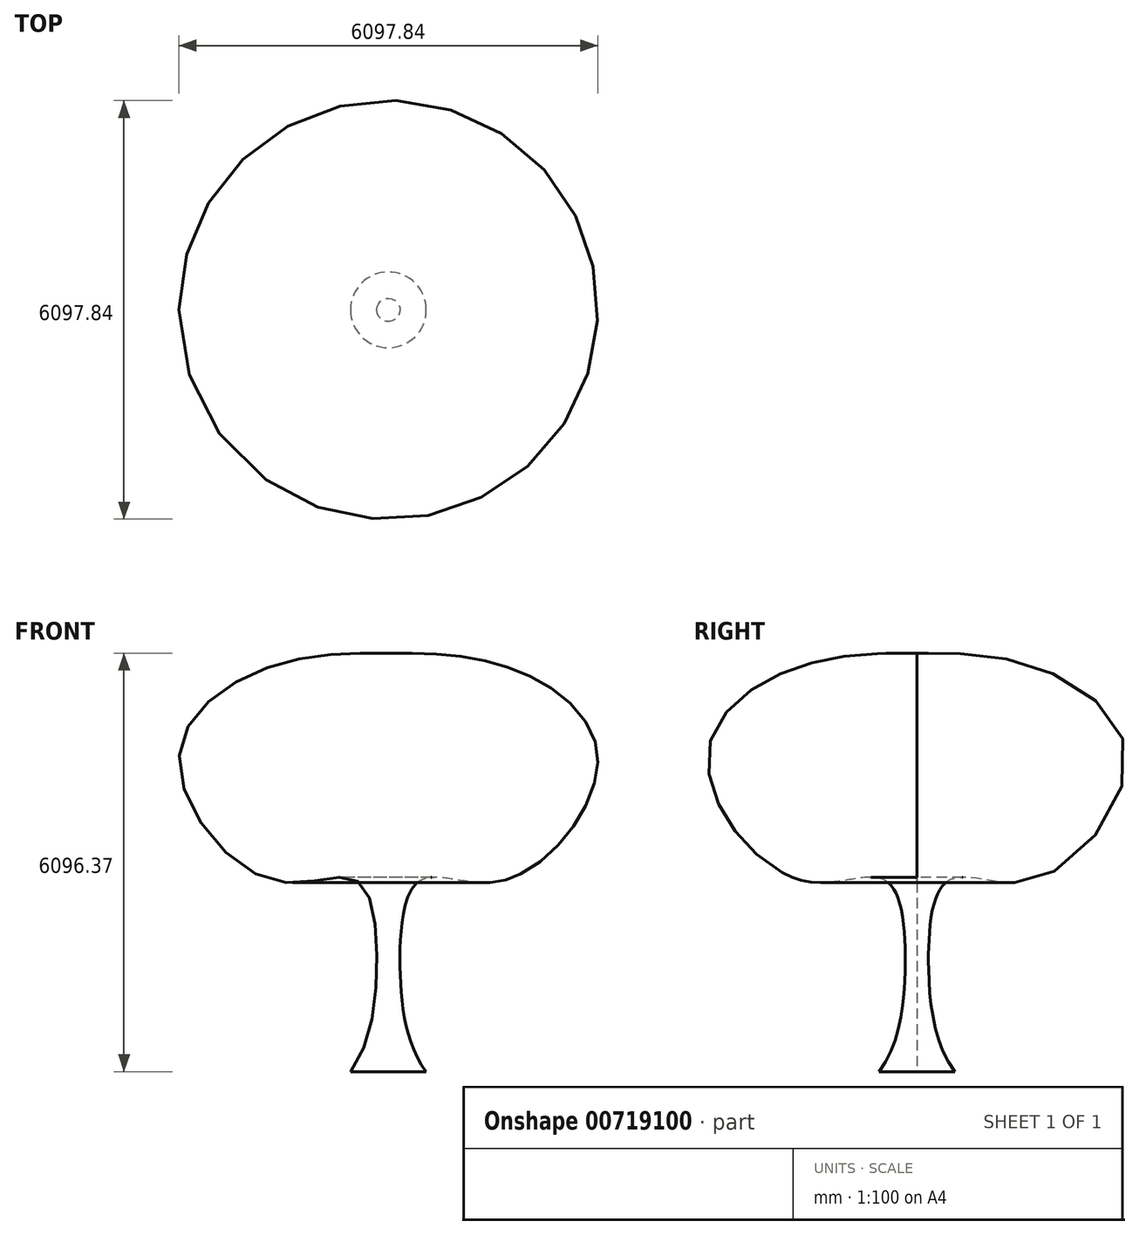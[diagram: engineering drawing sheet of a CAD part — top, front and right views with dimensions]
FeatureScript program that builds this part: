
annotation { "Feature Type Name" : "Feature", "Feature Type Description" : "" }
export const myFeature = defineFeature(function(context is Context, id is Id, definition is map)
    precondition{}
    {
        {
            var Q0;
            Q0=qCreatedBy(makeId("Front.planeOp"),FACE);
            var sketch = newSketch(context, id + "F0", { "sketchPlane" : qUnion([Q0])});
            skLineSegment(sketch, "E0", {"start": v(0, 0) * mm, "end": v(0, 6096) * mm});
            skFitSpline(sketch, "E1", {"points": [v(0, 6096) * mm, v(-1751, 5886.78) * mm, v(-3048, 4578.48) * mm, v(-1700.74, 2790.99) * mm, v(-484.2, 2797.13) * mm, v(-168.76, 1640.89) * mm, v(-551.41, 0) * mm], "startDerivative": vector(-9027.64, 26.57) * mm, "endDerivative": vector(-5444.11, -7117.56) * mm});
            skLineSegment(sketch, "E2", {"start": v(-551.41, 0) * mm, "end": v(0, 0) * mm});
            skSolve(sketch);
        }
        {
            var Q0;
            Q0=sQuery(id+"F0.wireOp",EDGE,"E1");
            var Q1;
            Q1=sQuery(id+"F0.wireOp",EDGE,"E0");
            revolve(context, id + "F1", {"bodyType" : ToolBodyType.SURFACE, "surfaceOperationType" : NewSurfaceOperationType.NEW, "surfaceEntities" : qUnion([Q0]), "axis" : qUnion([Q1]), "revolveType" : RevolveType.FULL});
        }
    });
